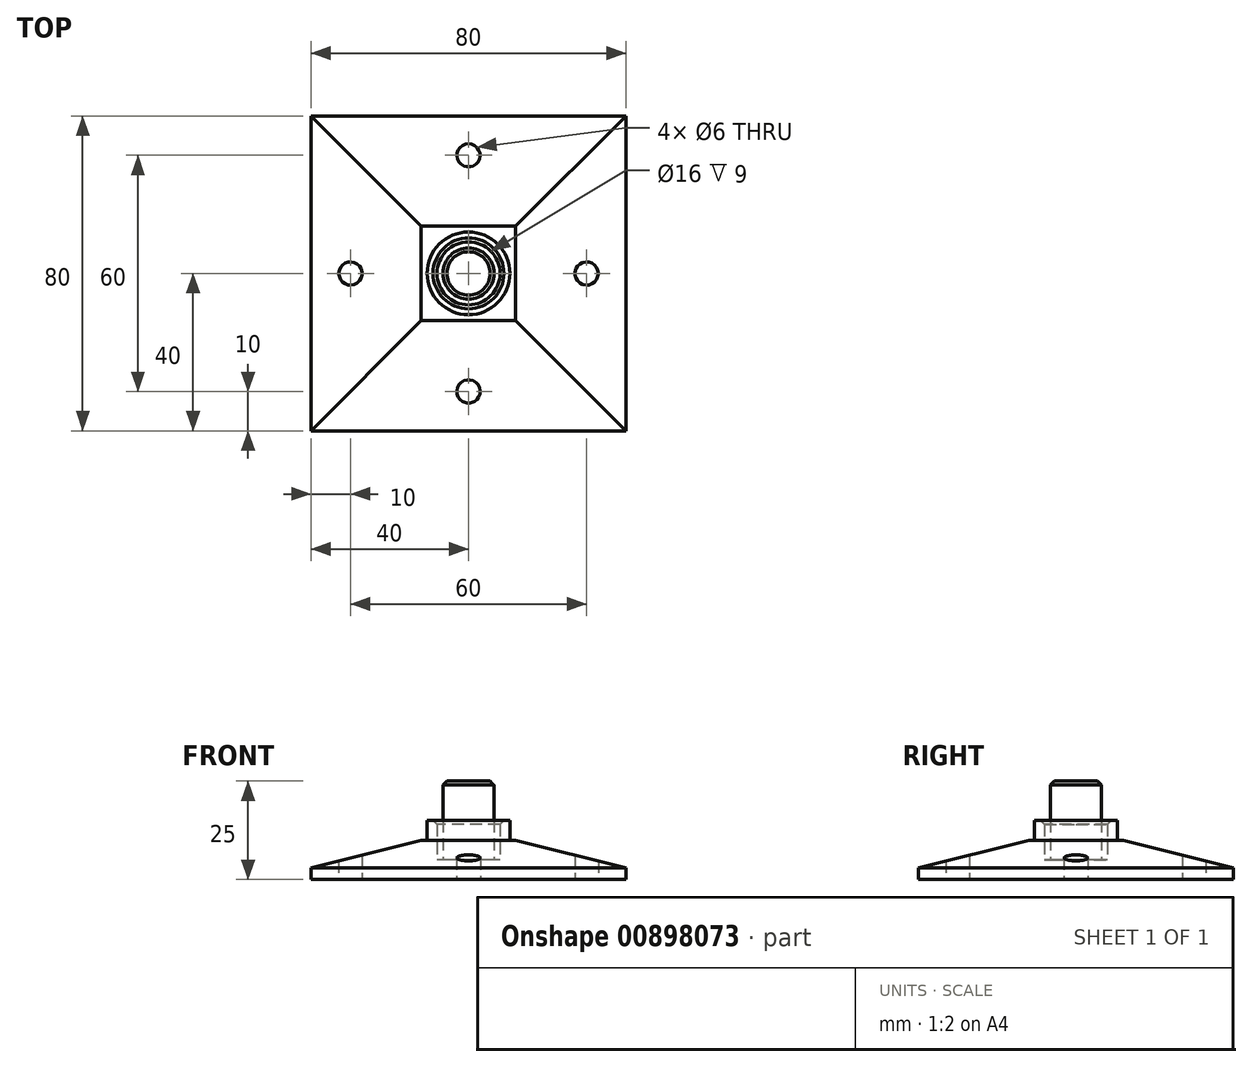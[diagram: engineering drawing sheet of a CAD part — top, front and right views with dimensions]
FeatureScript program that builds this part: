
annotation { "Feature Type Name" : "Feature", "Feature Type Description" : "" }
export const myFeature = defineFeature(function(context is Context, id is Id, definition is map)
    precondition{}
    {
        {
            var Q0;
            Q0=qCreatedBy(makeId("Top.planeOp"),FACE);
            var sketch = newSketch(context, id + "F0", { "sketchPlane" : qUnion([Q0])});
            skCircle(sketch, "E0", {"center": v(0, 0) * mm, "radius": 6.5 * mm});
            skCircle(sketch, "E1", {"center": v(0, 0) * mm, "radius": 8 * mm});
            skLineSegment(sketch, "E2.bottom", {"start": v(40, -40) * mm, "end": v(-40, -40) * mm});
            skLineSegment(sketch, "E2.top", {"start": v(40, 40) * mm, "end": v(-40, 40) * mm});
            skLineSegment(sketch, "E2.left", {"start": v(40, -40) * mm, "end": v(40, 40) * mm});
            skLineSegment(sketch, "E2.right", {"start": v(-40, -40) * mm, "end": v(-40, 40) * mm});
            skLineSegment(sketch, "E3", {"start": v(-40, 40) * mm, "end": v(40, -40) * mm});
            skLineSegment(sketch, "E4", {"start": v(40, 40) * mm, "end": v(-40, -40) * mm});
            skCircle(sketch, "E5", {"center": v(0, 0) * mm, "radius": 10.5 * mm});
            skPoint(sketch, "E6", {"position": v(-30, 0) * mm});
            skPoint(sketch, "E7", {"position": v(0, 30) * mm});
            skPoint(sketch, "E8", {"position": v(30, 0) * mm});
            skPoint(sketch, "E9", {"position": v(0, -30) * mm});
            skCircle(sketch, "E10", {"center": v(0, -30) * mm, "radius": 3 * mm});
            skCircle(sketch, "E11", {"center": v(-30, 0) * mm, "radius": 3 * mm});
            skCircle(sketch, "E12", {"center": v(0, 30) * mm, "radius": 3 * mm});
            skCircle(sketch, "E13", {"center": v(30, 0) * mm, "radius": 3 * mm});
            skSolve(sketch);
        }
        {
            var Q0;
            Q0 = qSketchRegion(id + "F0", true);
            extrude(context, id + "F1", {"entities" : qUnion([Q0]), "depth" : 10 * mm, "offsetDistance" : 25 * mm});
        }
        {
            var Q0;
            {var subQ0=sQuery(id+"F0.wireOp",EDGE,"E3");var subQ1=sQuery(id+"F0.wireOp",EDGE,"E1");var subQ2=makeQuery(id+"F0.imprint","INTERSECT",VERTEX,{"disambiguationData":[OD(0.0)],"derivedFrom":[subQ1,subQ0]});Q0=makeQuery(id+"F0.imprint","IMPRINT",FACE,{"disambiguationData":[TD([[makeQuery(id+"F0.imprint","IMPRINT",EDGE,{"disambiguationData":[TD([[subQ2,1.0]])],"derivedFrom":subQ1}),-1.0]])]});}
            var Q1;
            {var subQ0=sQuery(id+"F0.wireOp",EDGE,"E4");var subQ1=sQuery(id+"F0.wireOp",EDGE,"E1");var subQ2=makeQuery(id+"F0.imprint","INTERSECT",VERTEX,{"disambiguationData":[OD(0.0)],"derivedFrom":[subQ1,subQ0]});Q1=makeQuery(id+"F0.imprint","IMPRINT",FACE,{"disambiguationData":[TD([[makeQuery(id+"F0.imprint","IMPRINT",EDGE,{"disambiguationData":[TD([[subQ2,1.0]])],"derivedFrom":subQ1}),-1.0]])]});}
            var Q2;
            {var subQ0=sQuery(id+"F0.wireOp",EDGE,"E4");var subQ1=sQuery(id+"F0.wireOp",EDGE,"E1");var subQ2=makeQuery(id+"F0.imprint","INTERSECT",VERTEX,{"disambiguationData":[OD(1.0)],"derivedFrom":[subQ1,subQ0]});Q2=makeQuery(id+"F0.imprint","IMPRINT",FACE,{"disambiguationData":[TD([[makeQuery(id+"F0.imprint","IMPRINT",EDGE,{"disambiguationData":[TD([[subQ2,-1.0]])],"derivedFrom":subQ1}),-1.0]])]});}
            var Q3;
            {var subQ0=sQuery(id+"F0.wireOp",EDGE,"E3");var subQ1=sQuery(id+"F0.wireOp",EDGE,"E1");var subQ2=makeQuery(id+"F0.imprint","INTERSECT",VERTEX,{"disambiguationData":[OD(0.0)],"derivedFrom":[subQ1,subQ0]});Q3=makeQuery(id+"F0.imprint","IMPRINT",FACE,{"disambiguationData":[TD([[makeQuery(id+"F0.imprint","IMPRINT",EDGE,{"disambiguationData":[TD([[subQ2,-1.0]])],"derivedFrom":subQ1}),-1.0]])]});}
            extrude(context, id + "F2", {"entities" : qUnion([Q0, Q1, Q2, Q3]), "operationType" : NewBodyOperationType.ADD, "depth" : 15 * mm, "offsetDistance" : 25 * mm});
        }
        {
            var Q0;
            {var subQ0=sQuery(id+"F0.wireOp",EDGE,"E4");var subQ1=sQuery(id+"F0.wireOp",EDGE,"E0");var subQ2=makeQuery(id+"F0.imprint","INTERSECT",VERTEX,{"disambiguationData":[OD(0.0)],"derivedFrom":[subQ1,subQ0]});Q0=makeQuery(id+"F0.imprint","IMPRINT",FACE,{"disambiguationData":[TD([[makeQuery(id+"F0.imprint","IMPRINT",EDGE,{"disambiguationData":[TD([[subQ2,1.0]])],"derivedFrom":subQ1}),-1.0]])]});}
            var Q1;
            {var subQ0=sQuery(id+"F0.wireOp",EDGE,"E4");var subQ1=sQuery(id+"F0.wireOp",EDGE,"E0");var subQ2=makeQuery(id+"F0.imprint","INTERSECT",VERTEX,{"disambiguationData":[OD(1.0)],"derivedFrom":[subQ1,subQ0]});Q1=makeQuery(id+"F0.imprint","IMPRINT",FACE,{"disambiguationData":[TD([[makeQuery(id+"F0.imprint","IMPRINT",EDGE,{"disambiguationData":[TD([[subQ2,-1.0]])],"derivedFrom":subQ1}),-1.0]])]});}
            var Q2;
            {var subQ0=sQuery(id+"F0.wireOp",EDGE,"E3");var subQ1=sQuery(id+"F0.wireOp",EDGE,"E0");var subQ2=makeQuery(id+"F0.imprint","INTERSECT",VERTEX,{"disambiguationData":[OD(0.0)],"derivedFrom":[subQ1,subQ0]});Q2=makeQuery(id+"F0.imprint","IMPRINT",FACE,{"disambiguationData":[TD([[makeQuery(id+"F0.imprint","IMPRINT",EDGE,{"disambiguationData":[TD([[subQ2,1.0]])],"derivedFrom":subQ1}),-1.0]])]});}
            var Q3;
            {var subQ0=sQuery(id+"F0.wireOp",EDGE,"E3");var subQ1=sQuery(id+"F0.wireOp",EDGE,"E0");var subQ2=makeQuery(id+"F0.imprint","INTERSECT",VERTEX,{"disambiguationData":[OD(0.0)],"derivedFrom":[subQ1,subQ0]});Q3=makeQuery(id+"F0.imprint","IMPRINT",FACE,{"disambiguationData":[TD([[makeQuery(id+"F0.imprint","IMPRINT",EDGE,{"disambiguationData":[TD([[subQ2,-1.0]])],"derivedFrom":subQ1}),-1.0]])]});}
            extrude(context, id + "F3", {"entities" : qUnion([Q0, Q1, Q2, Q3]), "operationType" : NewBodyOperationType.ADD, "depth" : 5 * mm, "offsetDistance" : 25 * mm});
        }
        {
            var Q0;
            {var subQ0=sQuery(id+"F0.wireOp",EDGE,"E4");var subQ1=sQuery(id+"F0.wireOp",EDGE,"E0");var subQ2=makeQuery(id+"F0.imprint","INTERSECT",VERTEX,{"disambiguationData":[OD(0.0)],"derivedFrom":[subQ1,subQ0]});Q0=makeQuery(id+"F0.imprint","IMPRINT",FACE,{"disambiguationData":[TD([[makeQuery(id+"F0.imprint","IMPRINT",EDGE,{"disambiguationData":[TD([[subQ2,1.0]])],"derivedFrom":subQ1}),1.0]])]});}
            var Q1;
            {var subQ0=sQuery(id+"F0.wireOp",EDGE,"E4");var subQ1=sQuery(id+"F0.wireOp",EDGE,"E0");var subQ2=makeQuery(id+"F0.imprint","INTERSECT",VERTEX,{"disambiguationData":[OD(1.0)],"derivedFrom":[subQ1,subQ0]});Q1=makeQuery(id+"F0.imprint","IMPRINT",FACE,{"disambiguationData":[TD([[makeQuery(id+"F0.imprint","IMPRINT",EDGE,{"disambiguationData":[TD([[subQ2,-1.0]])],"derivedFrom":subQ1}),1.0]])]});}
            var Q2;
            {var subQ0=sQuery(id+"F0.wireOp",EDGE,"E3");var subQ1=sQuery(id+"F0.wireOp",EDGE,"E0");var subQ2=makeQuery(id+"F0.imprint","INTERSECT",VERTEX,{"disambiguationData":[OD(0.0)],"derivedFrom":[subQ1,subQ0]});Q2=makeQuery(id+"F0.imprint","IMPRINT",FACE,{"disambiguationData":[TD([[makeQuery(id+"F0.imprint","IMPRINT",EDGE,{"disambiguationData":[TD([[subQ2,-1.0]])],"derivedFrom":subQ1}),1.0]])]});}
            var Q3;
            {var subQ0=sQuery(id+"F0.wireOp",EDGE,"E3");var subQ1=sQuery(id+"F0.wireOp",EDGE,"E0");var subQ2=makeQuery(id+"F0.imprint","INTERSECT",VERTEX,{"disambiguationData":[OD(0.0)],"derivedFrom":[subQ1,subQ0]});Q3=makeQuery(id+"F0.imprint","IMPRINT",FACE,{"disambiguationData":[TD([[makeQuery(id+"F0.imprint","IMPRINT",EDGE,{"disambiguationData":[TD([[subQ2,1.0]])],"derivedFrom":subQ1}),1.0]])]});}
            extrude(context, id + "F4", {"entities" : qUnion([Q0, Q1, Q2, Q3]), "operationType" : NewBodyOperationType.ADD, "depth" : 25 * mm, "offsetDistance" : 25 * mm});
        }
        {
            var Q0;
            Q0=makeQuery(id+"F1.opExtrude","SWEPT_FACE",FACE,{"disambiguationData":[OSD([sQuery(id+"F0.wireOp",EDGE,"E2.bottom")])]});
            var sketch = newSketch(context, id + "F5", { "sketchPlane" : qUnion([Q0])});
            skLineSegment(sketch, "E14", {"start": v(-12, 10) * mm, "end": v(-40, 10) * mm});
            skLineSegment(sketch, "E15", {"start": v(12, 10) * mm, "end": v(40, 10) * mm});
            skLineSegment(sketch, "E16", {"start": v(-40, 10) * mm, "end": v(-40, 3) * mm});
            skLineSegment(sketch, "E17", {"start": v(-40, 3) * mm, "end": v(-12, 10) * mm});
            skLineSegment(sketch, "E18", {"start": v(12, 10) * mm, "end": v(40, 3) * mm});
            skLineSegment(sketch, "E19", {"start": v(40, 3) * mm, "end": v(40, 10) * mm});
            skSolve(sketch);
        }
        {
            var Q0;
            Q0=makeQuery(id+"F1.opExtrude","SWEPT_FACE",FACE,{"disambiguationData":[OSD([sQuery(id+"F0.wireOp",EDGE,"E2.right")])]});
            var sketch = newSketch(context, id + "F6", { "sketchPlane" : qUnion([Q0])});
            skLineSegment(sketch, "E20", {"start": v(-12, 10) * mm, "end": v(-40, 10) * mm});
            skLineSegment(sketch, "E21", {"start": v(12, 10) * mm, "end": v(40, 10) * mm});
            skLineSegment(sketch, "E22", {"start": v(40, 10) * mm, "end": v(40, 3) * mm});
            skLineSegment(sketch, "E23", {"start": v(40, 3) * mm, "end": v(12, 10) * mm});
            skLineSegment(sketch, "E24", {"start": v(-12, 10) * mm, "end": v(-40, 3) * mm});
            skLineSegment(sketch, "E25", {"start": v(-40, 3) * mm, "end": v(-40, 10) * mm});
            skSolve(sketch);
        }
        {
            var Q0;
            Q0 = qSketchRegion(id + "F5", true);
            extrude(context, id + "F7", {"entities" : qUnion([Q0]), "operationType" : NewBodyOperationType.REMOVE, "oppositeDirection" : true, "depth" : 80 * mm, "offsetDistance" : 25 * mm});
        }
        {
            var Q0;
            Q0 = qSketchRegion(id + "F6", true);
            extrude(context, id + "F8", {"entities" : qUnion([Q0]), "operationType" : NewBodyOperationType.REMOVE, "oppositeDirection" : true, "depth" : 80 * mm, "offsetDistance" : 25 * mm});
        }
        {
            var Q0;
            Q0=makeQuery(id+"F2.opExtrude","CAP_EDGE",EDGE,{"disambiguationData":[OSD([sQuery(id+"F0.wireOp",EDGE,"E1")])],"isStart":false});
            var Q1;
            Q1=makeQuery(id+"F4.opExtrude","CAP_EDGE",EDGE,{"disambiguationData":[OSD([sQuery(id+"F0.wireOp",EDGE,"E0")])],"isStart":false});
            chamfer(context, id + "F9", {"entities" : qUnion([Q0, Q1]), "width" : 1 * mm, "tangentPropagation" : true});
        }
    });
